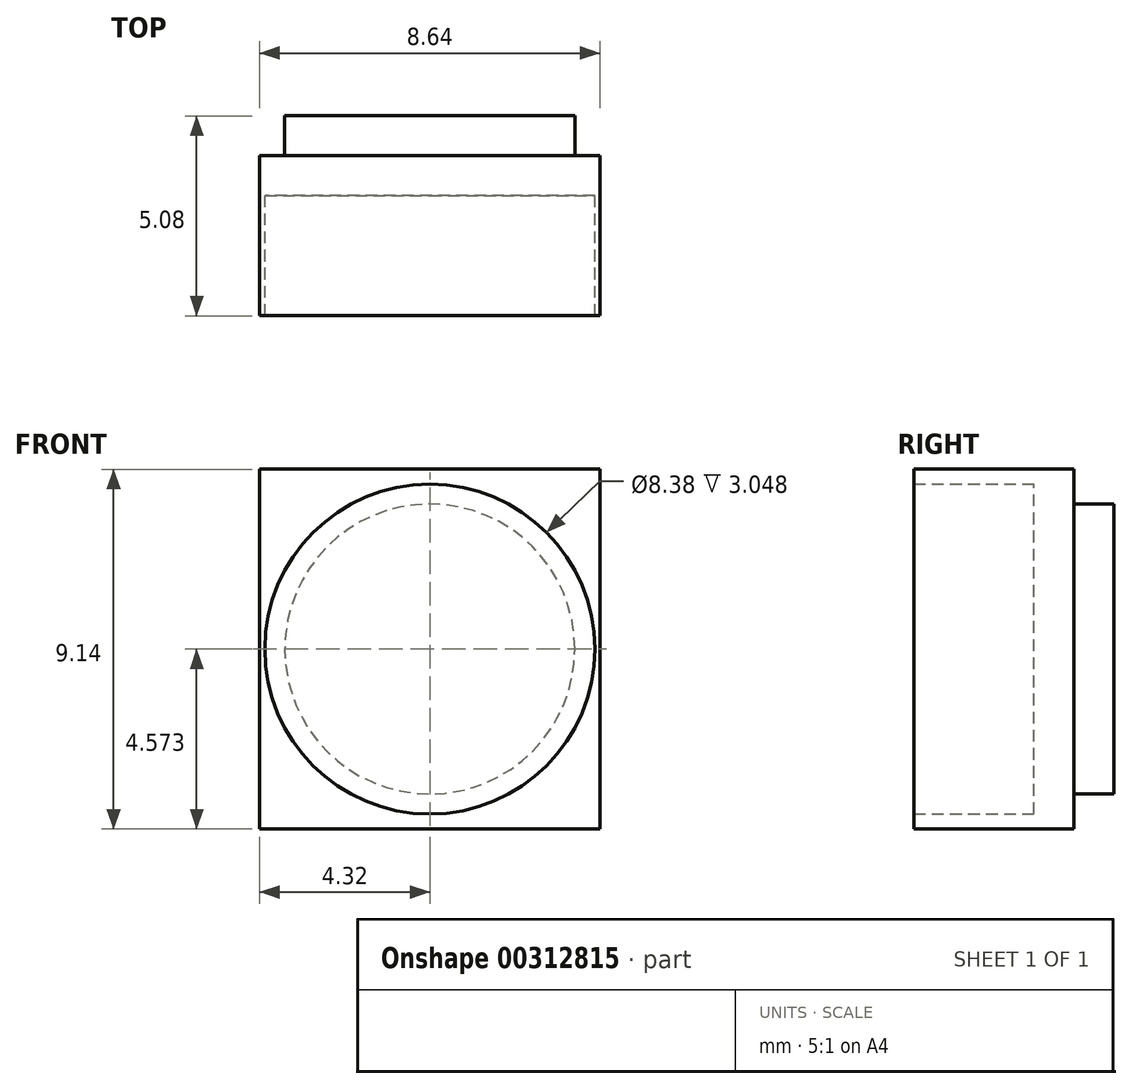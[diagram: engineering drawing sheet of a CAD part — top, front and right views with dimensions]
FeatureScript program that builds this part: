
annotation { "Feature Type Name" : "Feature", "Feature Type Description" : "" }
export const myFeature = defineFeature(function(context is Context, id is Id, definition is map)
    precondition{}
    {
        {
            var Q0;
            Q0=qCreatedBy(makeId("Front.planeOp"),FACE);
            var sketch = newSketch(context, id + "F0", { "sketchPlane" : qUnion([Q0])});
            skLineSegment(sketch, "E0.bottom", {"start": v(-4.32, -3.66) * mm, "end": v(4.32, -3.66) * mm});
            skLineSegment(sketch, "E0.top", {"start": v(-4.32, -12.8) * mm, "end": v(4.32, -12.8) * mm});
            skLineSegment(sketch, "E0.left", {"start": v(-4.32, -3.66) * mm, "end": v(-4.32, -12.8) * mm});
            skLineSegment(sketch, "E0.right", {"start": v(4.32, -3.66) * mm, "end": v(4.32, -12.8) * mm});
            skCircle(sketch, "E1", {"center": v(0, -8.23) * mm, "radius": 4.2 * mm});
            skCircle(sketch, "E2", {"center": v(0, -8.23) * mm, "radius": 3.68 * mm});
            skSolve(sketch);
        }
        {
            var Q0;
            Q0=makeQuery(id+"F0.imprint","IMPRINT",FACE,{"disambiguationData":[TD([[makeQuery(id+"F0.imprint","IMPRINT",EDGE,{"derivedFrom":sQuery(id+"F0.wireOp",EDGE,"E0.bottom")}),-1.0]])]});
            extrude(context, id + "F1", {"entities" : qUnion([Q0]), "depth" : 3.05 * mm});
        }
        {
            var Q0;
            Q0=makeQuery(id+"F0.imprint","IMPRINT",FACE,{"disambiguationData":[TD([[makeQuery(id+"F0.imprint","IMPRINT",EDGE,{"derivedFrom":sQuery(id+"F0.wireOp",EDGE,"E0.bottom")}),-1.0]])]});
            var Q1;
            Q1=makeQuery(id+"F0.imprint","IMPRINT",FACE,{"disambiguationData":[TD([[makeQuery(id+"F0.imprint","IMPRINT",EDGE,{"derivedFrom":sQuery(id+"F0.wireOp",EDGE,"E2")}),1.0]])]});
            var Q2;
            Q2=makeQuery(id+"F0.imprint","IMPRINT",FACE,{"disambiguationData":[TD([[makeQuery(id+"F0.imprint","IMPRINT",EDGE,{"derivedFrom":sQuery(id+"F0.wireOp",EDGE,"E1")}),1.0]])]});
            extrude(context, id + "F2", {"entities" : qUnion([Q0, Q1, Q2]), "operationType" : NewBodyOperationType.ADD, "depth" : -1.02 * mm});
        }
        {
            var Q0;
            Q0=makeQuery(id+"F0.imprint","IMPRINT",FACE,{"disambiguationData":[TD([[makeQuery(id+"F0.imprint","IMPRINT",EDGE,{"derivedFrom":sQuery(id+"F0.wireOp",EDGE,"E2")}),1.0]])]});
            extrude(context, id + "F3", {"entities" : qUnion([Q0]), "operationType" : NewBodyOperationType.ADD, "depth" : -2.03 * mm});
        }
    });
